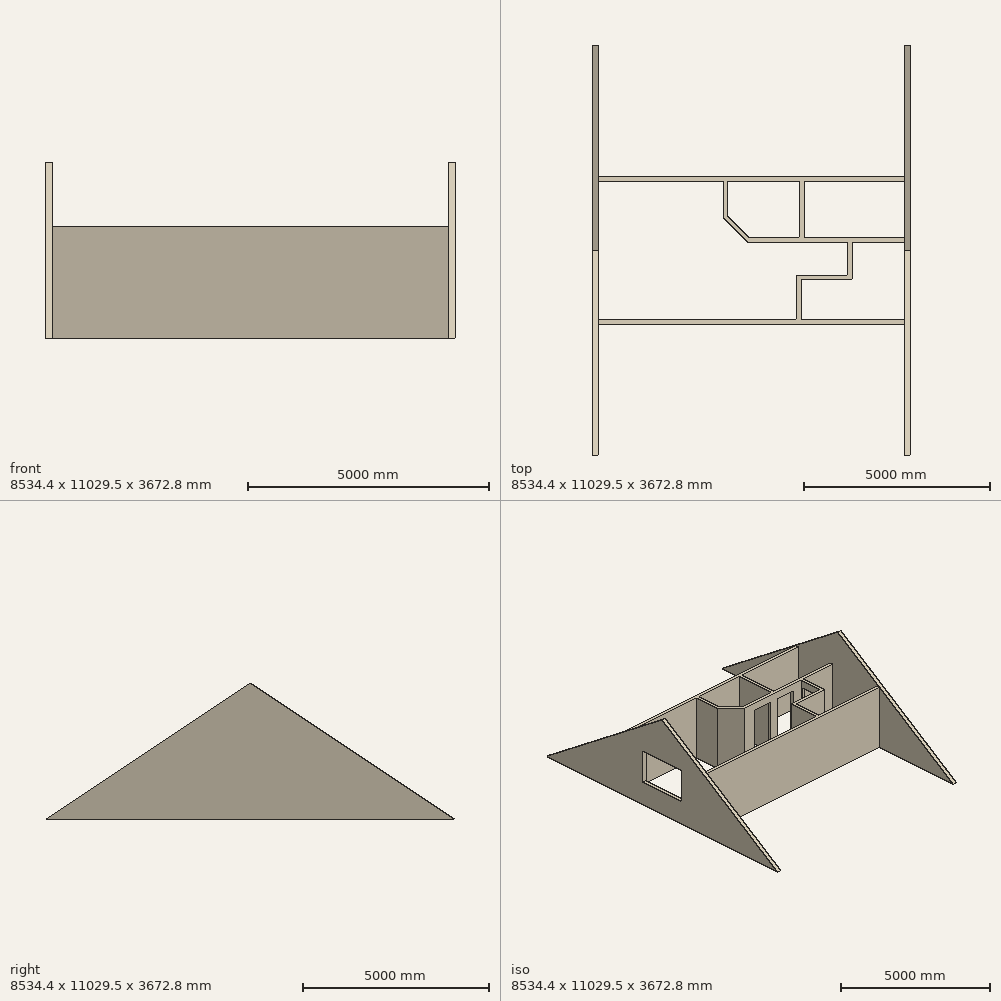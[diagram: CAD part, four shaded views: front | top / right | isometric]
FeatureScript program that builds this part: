
annotation { "Feature Type Name" : "Feature", "Feature Type Description" : "" }
export const myFeature = defineFeature(function(context is Context, id is Id, definition is map)
    precondition{}
    {
        {
            var Q0;
            Q0=qCreatedBy(makeId("Top.planeOp"),FACE);
            var sketch = newSketch(context, id + "F0", { "sketchPlane" : qUnion([Q0])});
            skLineSegment(sketch, "E0.bottom", {"start": v(-4114.8, 1866.9) * mm, "end": v(-762, 1866.9) * mm});
            skLineSegment(sketch, "E0.top", {"start": v(-4114.8, -1866.9) * mm, "end": v(1219.2, -1866.9) * mm});
            skLineSegment(sketch, "E0.left", {"start": v(-4114.8, 1866.9) * mm, "end": v(-4114.8, -1866.9) * mm});
            skLineSegment(sketch, "E0.right", {"start": v(4114.8, 1866.9) * mm, "end": v(4114.8, 350.52) * mm});
            skLineSegment(sketch, "E1.bottom", {"start": v(-4267.2, 1988.82) * mm, "end": v(4267.2, 1988.82) * mm});
            skLineSegment(sketch, "E1.top", {"start": v(-4267.2, -1988.82) * mm, "end": v(4267.2, -1988.82) * mm});
            skLineSegment(sketch, "E1.left", {"start": v(-4267.2, 1988.82) * mm, "end": v(-4267.2, -1988.82) * mm});
            skLineSegment(sketch, "E1.right", {"start": v(4267.2, 1988.82) * mm, "end": v(4267.2, -1988.82) * mm});
            skLineSegment(sketch, "E2", {"start": v(-762, 1866.9) * mm, "end": v(-762, 876.3) * mm});
            skLineSegment(sketch, "E3", {"start": v(-762, 876.3) * mm, "end": v(-114.3, 228.6) * mm});
            skLineSegment(sketch, "E4", {"start": v(-114.3, 228.6) * mm, "end": v(2590.8, 228.6) * mm});
            skLineSegment(sketch, "E5", {"start": v(-640.08, 1866.9) * mm, "end": v(-640.08, 926.8) * mm});
            skLineSegment(sketch, "E6", {"start": v(-640.08, 926.8) * mm, "end": v(-63.8, 350.52) * mm});
            skLineSegment(sketch, "E7", {"start": v(-63.8, 350.52) * mm, "end": v(4114.8, 350.52) * mm});
            skLineSegment(sketch, "E8", {"start": v(1301.5, 1866.9) * mm, "end": v(1301.5, 350.52) * mm});
            skLineSegment(sketch, "E9", {"start": v(1423.42, 1866.9) * mm, "end": v(1423.42, 350.52) * mm});
            skLineSegment(sketch, "E10", {"start": v(1219.2, -1866.9) * mm, "end": v(1219.2, -670.56) * mm});
            skLineSegment(sketch, "E11", {"start": v(1219.2, -670.56) * mm, "end": v(2590.8, -670.56) * mm});
            skLineSegment(sketch, "E12", {"start": v(2590.8, -670.56) * mm, "end": v(2590.8, 228.6) * mm});
            skLineSegment(sketch, "E13", {"start": v(1341.12, -1866.9) * mm, "end": v(1341.12, -792.48) * mm});
            skLineSegment(sketch, "E14", {"start": v(1341.12, -792.48) * mm, "end": v(2712.72, -792.48) * mm});
            skLineSegment(sketch, "E15", {"start": v(2712.72, -792.48) * mm, "end": v(2712.72, 228.6) * mm});
            skLineSegment(sketch, "E16.trimOffspring", {"start": v(-640.08, 1866.9) * mm, "end": v(1301.5, 1866.9) * mm});
            skLineSegment(sketch, "E17.trimOffspring", {"start": v(1423.42, 1866.9) * mm, "end": v(4114.8, 1866.9) * mm});
            skLineSegment(sketch, "E18.trimOffspring", {"start": v(2712.72, 228.6) * mm, "end": v(4114.8, 228.6) * mm});
            skLineSegment(sketch, "E19.trimOffspring", {"start": v(1341.12, -1866.9) * mm, "end": v(4114.8, -1866.9) * mm});
            skLineSegment(sketch, "E20.trimOffspring", {"start": v(4114.8, 228.6) * mm, "end": v(4114.8, -1866.9) * mm});
            skSolve(sketch);
        }
        {
            var Q0;
            Q0=makeQuery(id+"F0.imprint","IMPRINT",FACE,{"disambiguationData":[TD([[makeQuery(id+"F0.imprint","IMPRINT",EDGE,{"derivedFrom":sQuery(id+"F0.wireOp",EDGE,"E0.bottom")}),1.0]])]});
            extrude(context, id + "F1", {"entities" : qUnion([Q0]), "depth" : 2336.6 * mm});
        }
        {
            var Q0;
            Q0=makeQuery(id+"F1.opExtrude","SWEPT_FACE",FACE,{"disambiguationData":[OSD([sQuery(id+"F0.wireOp",EDGE,"E1.left")])]});
            var sketch = newSketch(context, id + "F2", { "sketchPlane" : qUnion([Q0])});
            skLineSegment(sketch, "E21.bottom", {"start": v(-914.4, 876.3) * mm, "end": v(914.4, 876.3) * mm});
            skLineSegment(sketch, "E21.top", {"start": v(-914.4, 2095.5) * mm, "end": v(914.4, 2095.5) * mm});
            skLineSegment(sketch, "E21.left", {"start": v(-914.4, 876.3) * mm, "end": v(-914.4, 2095.5) * mm});
            skLineSegment(sketch, "E21.right", {"start": v(914.4, 876.3) * mm, "end": v(914.4, 2095.5) * mm});
            skSolve(sketch);
        }
        {
            var Q0;
            Q0=makeQuery(id+"F2.imprint","IMPRINT",FACE,{"disambiguationData":[TD([[makeQuery(id+"F2.imprint","IMPRINT",EDGE,{"derivedFrom":sQuery(id+"F2.wireOp",EDGE,"E21.bottom")}),1.0]])]});
            extrude(context, id + "F3", {"entities" : qUnion([Q0]), "operationType" : NewBodyOperationType.REMOVE, "oppositeDirection" : true, "depth" : 152.4 * mm});
        }
        {
            var Q0;
            Q0=makeQuery(id+"F1.opExtrude","SWEPT_FACE",FACE,{"disambiguationData":[OSD([sQuery(id+"F0.wireOp",EDGE,"E4")])]});
            var sketch = newSketch(context, id + "F4", { "sketchPlane" : qUnion([Q0])});
            skLineSegment(sketch, "E22.bottom", {"start": v(1447.8, 2057.4) * mm, "end": v(2209.8, 2057.4) * mm});
            skLineSegment(sketch, "E22.top", {"start": v(1447.8, 0) * mm, "end": v(2209.8, 0) * mm});
            skLineSegment(sketch, "E22.left", {"start": v(1447.8, 2057.4) * mm, "end": v(1447.8, 0) * mm});
            skLineSegment(sketch, "E22.right", {"start": v(2209.8, 2057.4) * mm, "end": v(2209.8, 0) * mm});
            skLineSegment(sketch, "E23.bottom", {"start": v(381, 2057.4) * mm, "end": v(1143, 2057.4) * mm});
            skLineSegment(sketch, "E23.top", {"start": v(381, 0) * mm, "end": v(1143, 0) * mm});
            skLineSegment(sketch, "E23.left", {"start": v(381, 2057.4) * mm, "end": v(381, 0) * mm});
            skLineSegment(sketch, "E23.right", {"start": v(1143, 2057.4) * mm, "end": v(1143, 0) * mm});
            skSolve(sketch);
        }
        {
            var Q0;
            Q0=makeQuery(id+"F4.imprint","IMPRINT",FACE,{"disambiguationData":[TD([[makeQuery(id+"F4.imprint","IMPRINT",EDGE,{"derivedFrom":sQuery(id+"F4.wireOp",EDGE,"E22.bottom")}),-1.0]])]});
            var Q1;
            Q1=makeQuery(id+"F4.imprint","IMPRINT",FACE,{"disambiguationData":[TD([[makeQuery(id+"F4.imprint","IMPRINT",EDGE,{"derivedFrom":sQuery(id+"F4.wireOp",EDGE,"E23.bottom")}),-1.0]])]});
            extrude(context, id + "F5", {"entities" : qUnion([Q0, Q1]), "operationType" : NewBodyOperationType.REMOVE, "oppositeDirection" : true, "depth" : 121.92 * mm});
        }
        {
            var Q0;
            Q0=makeQuery(id+"F1.opExtrude","SWEPT_FACE",FACE,{"disambiguationData":[OSD([sQuery(id+"F0.wireOp",EDGE,"E12")])]});
            var sketch = newSketch(context, id + "F6", { "sketchPlane" : qUnion([Q0])});
            skLineSegment(sketch, "E24.bottom", {"start": v(-160.02, 0) * mm, "end": v(601.98, 0) * mm});
            skLineSegment(sketch, "E24.top", {"start": v(-160.02, 2057.4) * mm, "end": v(601.98, 2057.4) * mm});
            skLineSegment(sketch, "E24.left", {"start": v(-160.02, 0) * mm, "end": v(-160.02, 2057.4) * mm});
            skLineSegment(sketch, "E24.right", {"start": v(601.98, 0) * mm, "end": v(601.98, 2057.4) * mm});
            skSolve(sketch);
        }
        {
            var Q0;
            Q0=makeQuery(id+"F6.imprint","IMPRINT",FACE,{"disambiguationData":[TD([[makeQuery(id+"F6.imprint","IMPRINT",EDGE,{"derivedFrom":sQuery(id+"F6.wireOp",EDGE,"E24.bottom")}),-1.0]])]});
            extrude(context, id + "F7", {"entities" : qUnion([Q0]), "operationType" : NewBodyOperationType.REMOVE, "oppositeDirection" : true, "depth" : 152.4 * mm});
        }
        {
            var Q0;
            Q0=makeQuery(id+"F1.opExtrude","SWEPT_FACE",FACE,{"disambiguationData":[OSD([sQuery(id+"F0.wireOp",EDGE,"E1.left")])]});
            var sketch = newSketch(context, id + "F8", { "sketchPlane" : qUnion([Q0])});
            skLineSegment(sketch, "E25", {"start": v(-5514.77, 0) * mm, "end": v(5514.77, 0) * mm});
            skLineSegment(sketch, "E26", {"start": v(5514.77, 0) * mm, "end": v(0, 3672.84) * mm});
            skLineSegment(sketch, "E27", {"start": v(0, 3672.84) * mm, "end": v(-5514.77, 0) * mm});
            skLineSegment(sketch, "E28", {"start": v(0, 2336.6) * mm, "end": v(0, -2423.16) * mm, "construction": true});
            skLineSegment(sketch, "E29", {"start": v(-1756.47, -2423.16) * mm, "end": v(2184.7, -2423.16) * mm, "construction": true});
            skLineSegment(sketch, "E30", {"start": v(0, -2423.16) * mm, "end": v(0, 3672.84) * mm, "construction": true});
            skLineSegment(sketch, "E31", {"start": v(0, 3469.84) * mm, "end": v(304.8, 3469.84) * mm, "construction": true});
            skLineSegment(sketch, "E32", {"start": v(304.8, 3469.84) * mm, "end": v(0, 3469.84) * mm, "construction": true});
            skLineSegment(sketch, "E33", {"start": v(0, 3469.84) * mm, "end": v(-304.8, 3469.84) * mm, "construction": true});
            skLineSegment(sketch, "E34", {"start": v(-5486.4, 3291.16) * mm, "end": v(-5486.4, -1991.2) * mm, "construction": true});
            skLineSegment(sketch, "E35.MirrorCS", {"start": v(5486.4, 3291.16) * mm, "end": v(5486.4, -1991.2) * mm, "construction": true});
            skSolve(sketch);
        }
        {
            var Q0;
            {var subQ1=sQuery(id+"F8.wireOp",EDGE,"E26");Q0=makeQuery(id+"F8.imprint","IMPRINT",FACE,{"disambiguationData":[TD([[makeQuery(id+"F8.imprint","IMPRINT",EDGE,{"derivedFrom":subQ1}),1.0]])]});}
            extrude(context, id + "F9", {"entities" : qUnion([Q0]), "operationType" : NewBodyOperationType.ADD, "oppositeDirection" : true, "depth" : 152.4 * mm});
        }
        {
            var Q0;
            Q0=makeQuery(id+"F1.opExtrude","SWEPT_FACE",FACE,{"disambiguationData":[OSD([sQuery(id+"F0.wireOp",EDGE,"E1.right")])]});
            var sketch = newSketch(context, id + "F10", { "sketchPlane" : qUnion([Q0])});
            skLineSegment(sketch, "E36.0", {"start": v(-5514.77, 0) * mm, "end": v(0, 3672.84) * mm});
            skLineSegment(sketch, "E37.0", {"start": v(0, 3672.84) * mm, "end": v(5514.77, 0) * mm});
            skLineSegment(sketch, "E38", {"start": v(-5514.77, 0) * mm, "end": v(5514.77, 0) * mm});
            skSolve(sketch);
        }
        {
            var Q0;
            {var subQ5=sQuery(id+"F10.wireOp",EDGE,"E36.0");Q0=makeQuery(id+"F10.imprint","IMPRINT",FACE,{"disambiguationData":[TD([[makeQuery(id+"F10.imprint","IMPRINT",EDGE,{"derivedFrom":subQ5}),-1.0]])]});}
            extrude(context, id + "F11", {"entities" : qUnion([Q0]), "operationType" : NewBodyOperationType.ADD, "oppositeDirection" : true, "depth" : 152.4 * mm});
        }
    });
